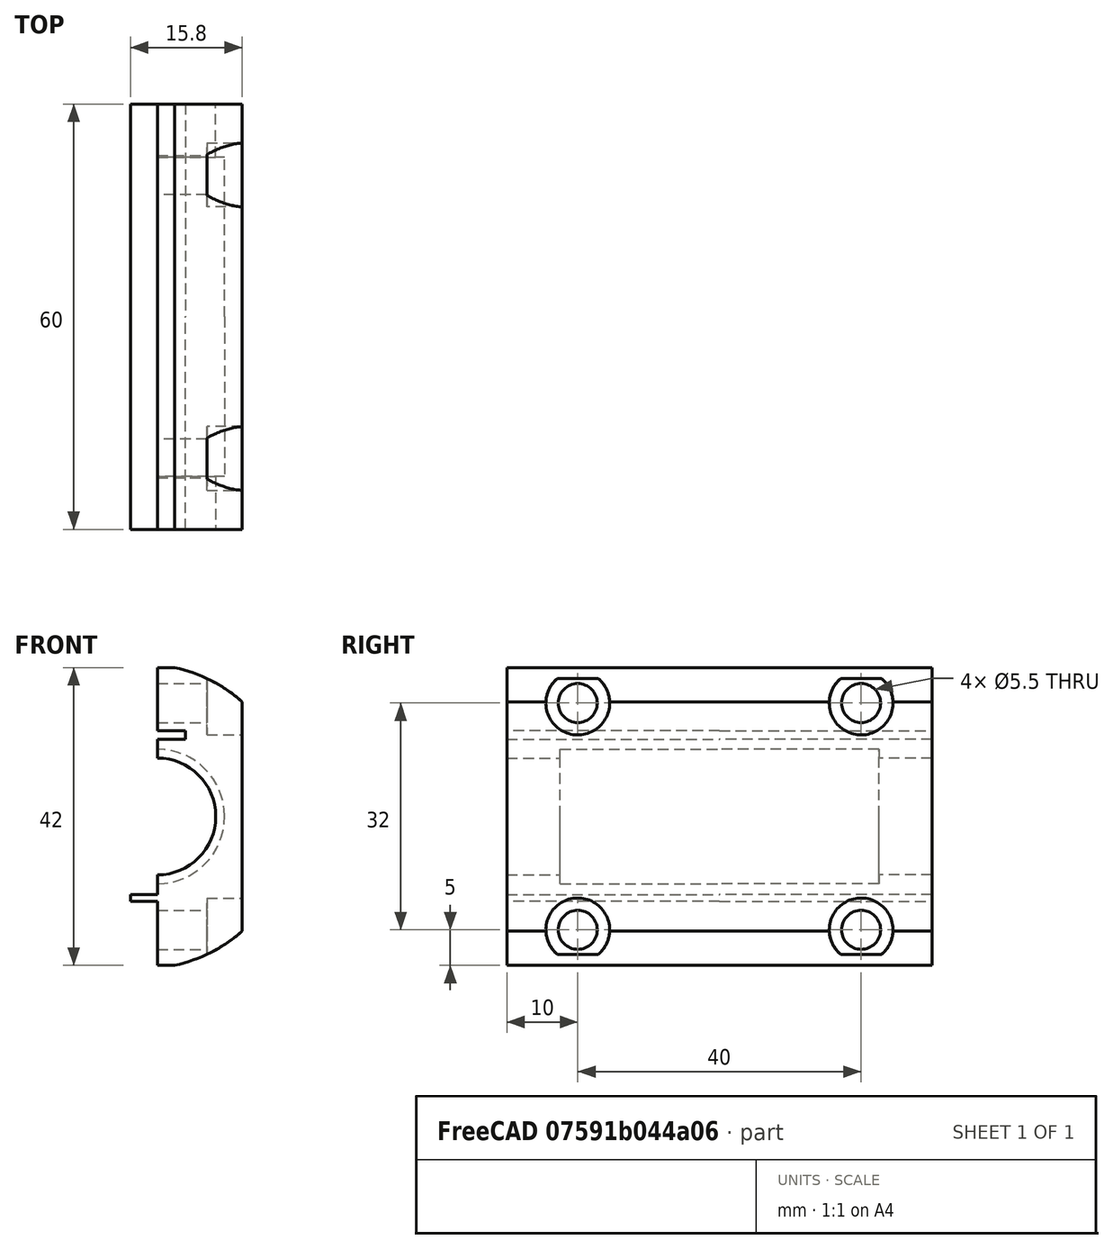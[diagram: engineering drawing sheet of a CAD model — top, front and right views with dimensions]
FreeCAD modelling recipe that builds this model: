
FCSTD DOCUMENT  (FreeCAD 0.21R33771 (Git))
Label: SunHeaterClamp
License: All rights reserved
LicenseURL: http://en.wikipedia.org/wiki/All_rights_reserved
objects: Sketcher::SketchObject×8, PartDesign::Pocket×6, PartDesign::Pad×2, PartDesign::Mirrored×1, PartDesign::Body×1, Mesh::Feature×1
note: 26 computed .brp shape members not serialized (recipe doc carries the construction recipe); baked Part::Feature solids carry a one-line shape summary decoded from their .brp

FEATURE [Sketcher::SketchObject] Sketch  label="FatEndSketch"
  FullyConstrained = true
  MapMode = 5
  Placement = pos=(0,0,0) rot=(1,0,0;1.5708rad)
  Support = -> [XZ_Plane]
  sketch-geometry (1):
    g0: Circle CenterX=0 CenterY=0 CenterZ=0 NormalX=0 NormalY=0 NormalZ=1 AngleXU=0 Radius=9.5
  constraints (2):
    c: Coincident(g0,g-1)
    c: Diameter(g0) = 19  'inner_dia'
FEATURE [Sketcher::SketchObject] Sketch001  label="ThinEndSketch"
  AttachmentOffset = pos=(0,0,22.5) rot=(0,0,1;0rad)
  FullyConstrained = true
  MapMode = 5
  Placement = pos=(0,-22.5,5e-15) rot=(1,0,0;1.5708rad)
  Support = -> [XZ_Plane]
  sketch-geometry (1):
    g0: Circle CenterX=0 CenterY=0 CenterZ=0 NormalX=0 NormalY=0 NormalZ=1 AngleXU=0 Radius=8.25
  constraints (2):
    c: Coincident(g0,g-1)
    c: Diameter(g0) = 16.5  'thinDia'
FEATURE [Sketcher::SketchObject] Sketch002  label="MainBodySketch"
  FullyConstrained = true
  MapMode = 5
  Placement = pos=(0,0,0) rot=(0.57735,0.57735,0.57735;2.0944rad)
  Support = -> [YZ_Plane]
  sketch-geometry (4):
    g0: LineSegment StartX=-30 StartY=21 StartZ=0 EndX=0 EndY=21 EndZ=0
    g1: LineSegment StartX=0 StartY=21 StartZ=0 EndX=0 EndY=-21 EndZ=0
    g2: LineSegment StartX=0 StartY=-21 StartZ=0 EndX=-30 EndY=-21 EndZ=0
    g3: LineSegment StartX=-30 StartY=-21 StartZ=0 EndX=-30 EndY=21 EndZ=0
  constraints (11):
    c: Coincident(g0,g1)
    c: Coincident(g1,g2)
    c: Coincident(g2,g3)
    c: Coincident(g3,g0)
    c: Horizontal(g0)
    c: Horizontal(g2)
    c: Vertical(g1)
    c: Vertical(g3)
    c: DistanceX(g0,g0) = 30
    c: DistanceY(g3,g3) = 42
    c: Symmetric(g0,g1,g-1)
FEATURE [PartDesign::Pad] Pad  label="MainBodyPad"
  Direction = (1,-2e-16,3e-16)
  Length = 12
  Length2 = 10
  Placement = pos=(0,0,0) rot=(1,1,1;2.0944rad)
  Profile = -> Sketch002
  ReferenceAxis = -> Sketch002 [N_Axis]
  Type = 0
FEATURE [PartDesign::Pocket] Pocket  label="FatPocket"
  BaseFeature = -> Pad
  Direction = (0,1,-2e-16)
  Length = 22.5
  Length2 = 5
  Placement = pos=(0,0,0) rot=(1,1,1;2.0944rad)
  Profile = -> Sketch
  ReferenceAxis = -> Sketch [N_Axis]
  Reversed = true
  Type = 0
FEATURE [PartDesign::Pocket] Pocket001  label="ThinPocket"
  BaseFeature = -> Pocket
  Direction = (0,1,-2e-16)
  Length = 20
  Length2 = 5
  Placement = pos=(0,0,0) rot=(1,1,1;2.0944rad)
  Profile = -> Sketch001
  ReferenceAxis = -> Sketch001 [N_Axis]
  Reversed = true
  Type = 1
FEATURE [Sketcher::SketchObject] Sketch003  label="SkrewHeadSketch"
  FullyConstrained = true
  MapMode = 5
  Placement = pos=(12,-1.07e-14,6.7e-15) rot=(0.57735,0.57735,0.57735;2.0944rad)
  Support = -> [Pocket001]
  sketch-geometry (2):
    g0: Circle CenterX=-20 CenterY=16 CenterZ=0 NormalX=0 NormalY=0 NormalZ=1 AngleXU=0 Radius=4.5
    g1: Circle CenterX=-20 CenterY=-16 CenterZ=0 NormalX=0 NormalY=0 NormalZ=1 AngleXU=0 Radius=4.5
  constraints (5):
    c: Diameter(g0) = 9
    c: DistanceX(g0,g-1) = 20
    c: Equal(g1,g0)
    c: Symmetric(g0,g1,g-1)
    c: DistanceY(g1,g0) = 32
FEATURE [PartDesign::Pocket] Pocket002  label="SkrewHeadPocket"
  BaseFeature = -> Pocket001
  Direction = (-1,8e-16,-6e-16)
  Length = 5
  Length2 = 5
  Placement = pos=(0,0,0) rot=(1,1,1;2.0944rad)
  Profile = -> Sketch003
  ReferenceAxis = -> Sketch003 [N_Axis]
  Type = 0
FEATURE [Sketcher::SketchObject] Sketch004  label="SkrewSketch"
  FullyConstrained = true
  MapMode = 5
  Placement = pos=(12,-1.33e-14,8e-15) rot=(0.57735,0.57735,0.57735;2.0944rad)
  Support = -> [Pocket002]
  sketch-geometry (2):
    g0: Circle CenterX=-20 CenterY=16 CenterZ=0 NormalX=0 NormalY=0 NormalZ=1 AngleXU=0 Radius=2.75
    g1: Circle CenterX=-20 CenterY=-16 CenterZ=0 NormalX=0 NormalY=0 NormalZ=1 AngleXU=0 Radius=2.75
  constraints (5):
    c: Symmetric(g0,g1,g-1)
    c: DistanceX(g0,g-1) = 20
    c: DistanceY(g1,g0) = 32
    c: Equal(g0,g1)
    c: Diameter(g0) = 5.5
FEATURE [PartDesign::Pocket] Pocket003  label="SkrewPocket"
  BaseFeature = -> Pocket002
  Direction = (-1,1.1e-15,-7e-16)
  Length = 5
  Length2 = 5
  Placement = pos=(0,0,0) rot=(1,1,1;2.0944rad)
  Profile = -> Sketch004
  ReferenceAxis = -> Sketch004 [N_Axis]
  Type = 1
FEATURE [Sketcher::SketchObject] Sketch005  label="SmoothInsertSketch"
  FullyConstrained = true
  MapMode = 5
  Placement = pos=(0,0,0) rot=(0.57735,0.57735,0.57735;2.0944rad)
  Support = -> [YZ_Plane]
  sketch-geometry (4):
    g0: LineSegment StartX=0 StartY=-11 StartZ=0 EndX=0 EndY=-12 EndZ=0
    g1: LineSegment StartX=0 StartY=-12 StartZ=0 EndX=-30 EndY=-12 EndZ=0
    g2: LineSegment StartX=-30 StartY=-11 StartZ=0 EndX=0 EndY=-11 EndZ=0
    g3: LineSegment StartX=-30 StartY=-11 StartZ=0 EndX=-30 EndY=-12 EndZ=0
  constraints (12):
    c: Coincident(g0,g1)
    c: Horizontal(g1)
    c: Vertical(g0)
    c: PointOnObject(g0,g-2)
    c: DistanceY(g0,g-1) = 11
    c: Coincident(g2,g0)
    c: Horizontal(g2)
    c: DistanceY(g0,g0) = 1
    c: DistanceX(g1,g1) = 30
    c: Coincident(g2,g3)
    c: Coincident(g3,g1)
    c: Vertical(g3)
FEATURE [PartDesign::Pad] Pad001  label="SmoothInsertPad"
  BaseFeature = -> Pocket003
  Direction = (1,-2e-16,3e-16)
  Length = 3.8
  Length2 = 10
  Placement = pos=(0,0,0) rot=(1,1,1;2.0944rad)
  Profile = -> Sketch005
  ReferenceAxis = -> Sketch005 [N_Axis]
  Reversed = true
  Type = 0
FEATURE [Sketcher::SketchObject] Sketch006  label="SmoothOutsertSketch"
  FullyConstrained = true
  MapMode = 5
  Placement = pos=(0,0,0) rot=(0.57735,0.57735,0.57735;2.0944rad)
  Support = -> [YZ_Plane]
  sketch-geometry (4):
    g0: LineSegment StartX=0 StartY=10.9 StartZ=0 EndX=0 EndY=12.1 EndZ=0
    g1: LineSegment StartX=0 StartY=12.1 StartZ=0 EndX=-30 EndY=12.1 EndZ=0
    g2: LineSegment StartX=-30 StartY=10.9 StartZ=0 EndX=0 EndY=10.9 EndZ=0
    g3: LineSegment StartX=-30 StartY=12.1 StartZ=0 EndX=-30 EndY=10.9 EndZ=0
  constraints (12):
    c: Coincident(g0,g1)
    c: Horizontal(g1)
    c: Vertical(g0)
    c: PointOnObject(g0,g-2)
    c: DistanceY(g-1,g0) = 10.9
    c: DistanceY(g0,g0) = 1.2
    c: Coincident(g2,g0)
    c: Horizontal(g2)
    c: DistanceX(g1,g1) = 30
    c: Coincident(g1,g3)
    c: Coincident(g3,g2)
    c: Vertical(g3)
FEATURE [PartDesign::Pocket] Pocket004  label="SmoothOutsertPocket"
  BaseFeature = -> Pad001
  Direction = (-1,2e-16,-3e-16)
  Length = 4
  Length2 = 5
  Placement = pos=(0,0,0) rot=(1,1,1;2.0944rad)
  Profile = -> Sketch006
  ReferenceAxis = -> Sketch006 [N_Axis]
  Reversed = true
  Type = 0
FEATURE [Sketcher::SketchObject] Sketch007
  FullyConstrained = true
  MapMode = 5
  Placement = pos=(0,0,0) rot=(1,0,0;1.5708rad)
  Support = -> [XZ_Plane]
  sketch-geometry (6):
    g0: Circle CenterX=-2.15 CenterY=0 CenterZ=0 NormalX=0 NormalY=0 NormalZ=1 AngleXU=0 Radius=21.5
    g1: LineSegment StartX=-27.5 StartY=27.5 StartZ=0 EndX=-27.5 EndY=-27.5 EndZ=0
    g2: LineSegment StartX=-27.5 StartY=-27.5 StartZ=0 EndX=27.5 EndY=-27.5 EndZ=0
    g3: LineSegment StartX=27.5 StartY=-27.5 StartZ=0 EndX=27.5 EndY=27.5 EndZ=0
    g4: LineSegment StartX=27.5 StartY=27.5 StartZ=0 EndX=-27.5 EndY=27.5 EndZ=0
    g5: GeomPoint X=0 Y=0 Z=0
  constraints (15):
    c: PointOnObject(g0,g-1)
    c: Coincident(g1,g2)
    c: Coincident(g2,g3)
    c: Coincident(g3,g4)
    c: Coincident(g4,g1)
    c: Horizontal(g2)
    c: Horizontal(g4)
    c: Vertical(g1)
    c: Vertical(g3)
    c: Symmetric(g2,g1,g5)
    c: Coincident(g5,g-1)
    c: Equal(g4,g3)
    c: DistanceX(g4,g4) = 55
    c: Diameter(g0) = 43
    c: DistanceX(g0,g5) = 2.15
FEATURE [PartDesign::Pocket] Pocket005
  BaseFeature = -> Pocket004
  Direction = (0,1,-2e-16)
  Length = 5
  Length2 = 5
  Placement = pos=(0,0,0) rot=(1,1,1;2.0944rad)
  Profile = -> Sketch007
  ReferenceAxis = -> Sketch007 [N_Axis]
  Reversed = true
  Type = 1
FEATURE [PartDesign::Mirrored] Mirrored
  BaseFeature = -> Pocket005
  MirrorPlane = -> Sketch002 [V_Axis]
  Originals = -> [Pad,Pocket,Pocket001,Pocket002,Pocket003,Pad001,Pocket004,Pocket005]
  Placement = pos=(0,0,0) rot=(1,1,1;2.0944rad)
FEATURE [PartDesign::Body] Body
  Group = -> [Sketch002,Sketch,Sketch001,Pad,Pocket,Pocket001,Sketch003,Pocket002,Sketch004,Pocket003,Sketch005,Pad001,Sketch006,Pocket004,Sketch007,Pocket005,Mirrored]
  Origin = -> Origin
  Tip = -> Mirrored
FEATURE [Mesh::Feature] Mesh  label="Mirrored (Meshed)"
